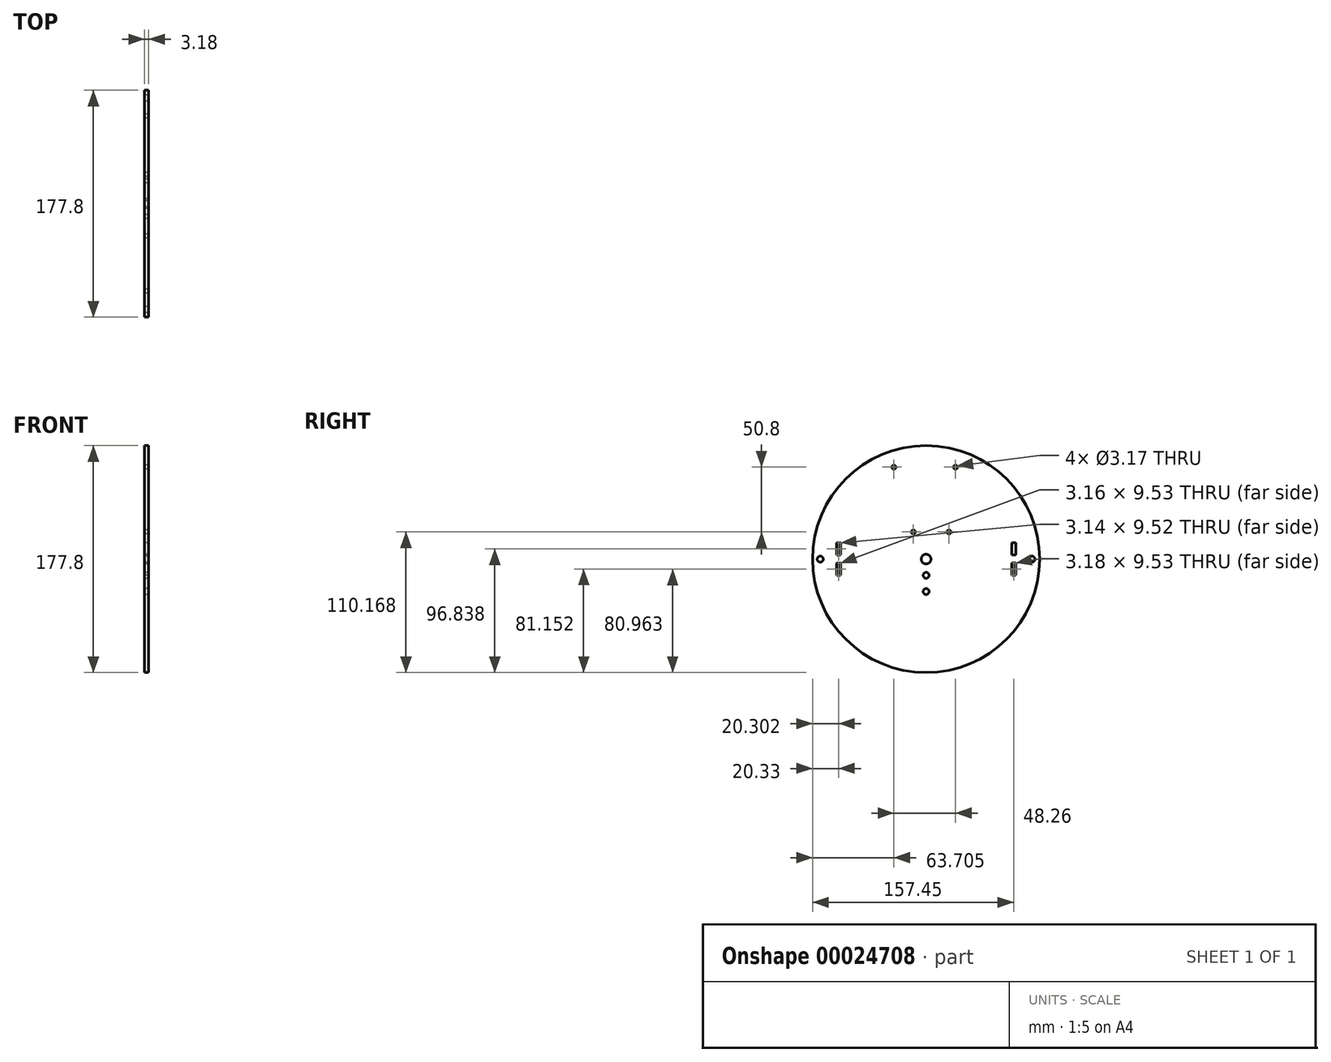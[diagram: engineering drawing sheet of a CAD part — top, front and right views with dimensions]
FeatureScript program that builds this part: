
annotation { "Feature Type Name" : "Feature", "Feature Type Description" : "" }
export const myFeature = defineFeature(function(context is Context, id is Id, definition is map)
    precondition{}
    {
        {
            var Q0;
            Q0=qCreatedBy(makeId("Right.planeOp"),FACE);
            var sketch = newSketch(context, id + "F0", { "sketchPlane" : qUnion([Q0])});
            skCircle(sketch, "E0", {"center": v(-201.47, 13.14) * mm, "radius": 88.9 * mm});
            skLineSegment(sketch, "E1.direction1", {"start": v(-132.89, 25.84) * mm, "end": v(-270.05, 25.84) * mm, "construction": true});
            skLineSegment(sketch, "E2", {"start": v(-201.47, 13.14) * mm, "end": v(-132.9, 13.31) * mm});
            skLineSegment(sketch, "E3", {"start": v(-201.47, 13.14) * mm, "end": v(-270.05, 13.14) * mm});
            skCircle(sketch, "E4.MirrorC", {"center": v(-211.42, 34.4) * mm, "radius": 1.59 * mm});
            skCircle(sketch, "E5", {"center": v(-201.47, 13.14) * mm, "radius": 3.81 * mm});
            skLineSegment(sketch, "E6", {"start": v(-132.9, 13.31) * mm, "end": v(-118.6, 13.14) * mm});
            skCircle(sketch, "E7.MirrorC", {"center": v(-226.66, 85.2) * mm, "radius": 1.59 * mm});
            skCircle(sketch, "E8.MirrorC", {"center": v(-178.4, 85.2) * mm, "radius": 1.59 * mm});
            skCircle(sketch, "E9.MirrorC", {"center": v(-183.48, 34.4) * mm, "radius": 1.59 * mm});
            skLineSegment(sketch, "E10", {"start": v(-134.48, 25.84) * mm, "end": v(-131.34, 25.84) * mm});
            skLineSegment(sketch, "E11.right", {"start": v(-271.62, 0.44) * mm, "end": v(-271.62, 9.97) * mm});
            skLineSegment(sketch, "E12", {"start": v(-271.62, 0.44) * mm, "end": v(-268.46, 0.44) * mm});
            skCircle(sketch, "E13", {"center": v(-201.47, 0.44) * mm, "radius": 2.31 * mm});
            skCircle(sketch, "E14", {"center": v(-201.47, -12.26) * mm, "radius": 2.31 * mm});
            skLineSegment(sketch, "E15.left", {"start": v(-271.64, 25.84) * mm, "end": v(-271.64, 16.32) * mm});
            skLineSegment(sketch, "E15.right", {"start": v(-268.5, 25.84) * mm, "end": v(-268.5, 16.32) * mm});
            skLineSegment(sketch, "E16", {"start": v(-271.64, 25.84) * mm, "end": v(-268.5, 25.84) * mm});
            skLineSegment(sketch, "E11.left", {"start": v(-268.46, 0.44) * mm, "end": v(-268.46, 9.97) * mm});
            skCircle(sketch, "E17", {"center": v(-284.34, 13.14) * mm, "radius": 2.35 * mm});
            skLineSegment(sketch, "E18.left", {"start": v(-134.48, 25.84) * mm, "end": v(-134.48, 16.5) * mm});
            skLineSegment(sketch, "E18.right", {"start": v(-131.34, 25.84) * mm, "end": v(-131.34, 16.5) * mm});
            skLineSegment(sketch, "E19", {"start": v(-134.5, 0.63) * mm, "end": v(-131.33, 0.63) * mm});
            skLineSegment(sketch, "E20.top", {"start": v(-131.33, 10.15) * mm, "end": v(-134.5, 10.15) * mm});
            skLineSegment(sketch, "E20.right", {"start": v(-134.5, 0.63) * mm, "end": v(-134.5, 10.15) * mm});
            skLineSegment(sketch, "E20.left", {"start": v(-131.33, 0.63) * mm, "end": v(-131.33, 10.15) * mm});
            skLineSegment(sketch, "E15.top", {"start": v(-271.64, 16.32) * mm, "end": v(-268.5, 16.32) * mm});
            skLineSegment(sketch, "E11.top", {"start": v(-268.46, 9.97) * mm, "end": v(-271.62, 9.97) * mm});
            skLineSegment(sketch, "E18.top", {"start": v(-134.48, 16.5) * mm, "end": v(-131.34, 16.5) * mm});
            skCircle(sketch, "E21", {"center": v(-118.6, 13.14) * mm, "radius": 2.35 * mm});
            skSolve(sketch);
        }
        {
            var Q0;
            Q0 = qSketchRegion(id + "F0", true);
            extrude(context, id + "F1", {"entities" : qUnion([Q0]), "depth" : 3.17 * mm});
        }
    });
